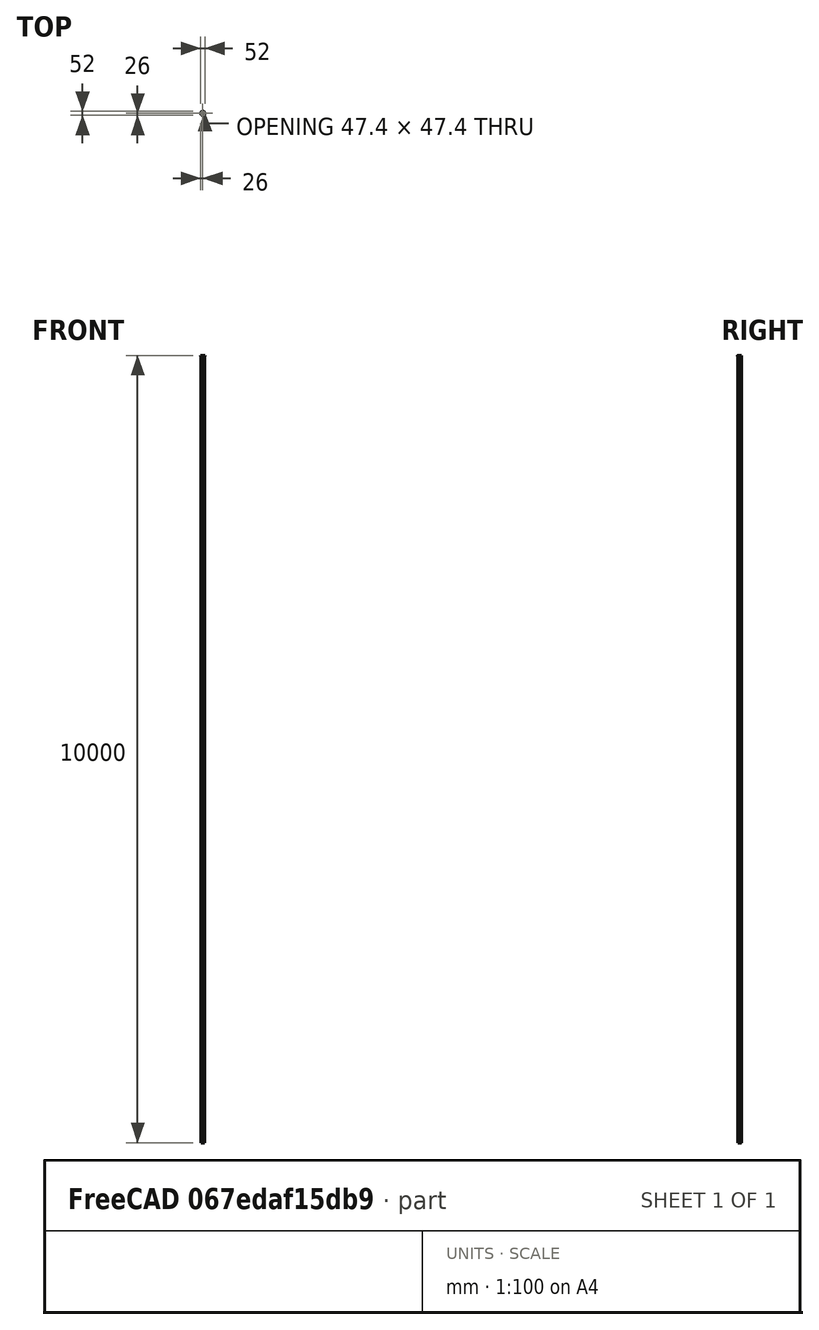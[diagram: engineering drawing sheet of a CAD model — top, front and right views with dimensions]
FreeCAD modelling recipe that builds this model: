
FCSTD DOCUMENT  (FreeCAD 0.16R)
Label: FWspacer
License: All rights reserved
LicenseURL: http://en.wikipedia.org/wiki/All_rights_reserved
objects: Sketcher::SketchObject×3, PartDesign::Pad×2, PartDesign::Pocket×1, PartDesign::PolarPattern×1, Mesh::Feature×1
note: 10 computed .brp shape members not serialized (recipe doc carries the construction recipe); baked Part::Feature solids carry a one-line shape summary decoded from their .brp

FEATURE [Sketcher::SketchObject] Sketch
  sketch-geometry (1):
    g0: Circle CenterX=0 CenterY=0 CenterZ=0 NormalX=0 NormalY=0 NormalZ=1 Radius=26
  constraints (2):
    c: Coincident(g0,g-1)
    c: Radius(g0) = 26
FEATURE [PartDesign::Pad] Pad
  Length = 5
  Length2 = 100
  Sketch = -> Sketch
  Type = 0
FEATURE [Sketcher::SketchObject] Sketch001
  Placement = pos=(0,0,5) rot=(0,0,1;0rad)
  Support = -> Pad [Face3]
  sketch-geometry (1):
    g0: Circle CenterX=0 CenterY=0 CenterZ=0 NormalX=0 NormalY=0 NormalZ=1 Radius=22.7
  constraints (2):
    c: Coincident(g0,g-1)
    c: Radius(g0) = 22.7
FEATURE [PartDesign::Pocket] Pocket
  Length = 5
  Sketch = -> Sketch001
  Type = 1
FEATURE [Sketcher::SketchObject] Sketch002
  ExternalGeometry = -> [Pocket]
  Placement = pos=(0,0,5) rot=(0,0,1;0rad)
  Support = -> Pocket [Face3]
  sketch-geometry (12):
    g0: LineSegment StartX=1.49899 StartY=22.4905 StartZ=0 EndX=1.49899 EndY=22.0946 EndZ=0
    g1: LineSegment StartX=1.10438 StartY=21.7 StartZ=0 EndX=-1.09517 EndY=21.7 EndZ=0
    g2: LineSegment StartX=-1.50098 StartY=22.1058 StartZ=0 EndX=-1.50098 EndY=22.3048 EndZ=0
    g3: LineSegment StartX=-1.89617 StartY=22.7 StartZ=0 EndX=-3 EndY=22.7 EndZ=0
    g4: LineSegment StartX=3 StartY=22.7 StartZ=0 EndX=3 EndY=23.7 EndZ=0
    g5: LineSegment StartX=3 StartY=23.7 StartZ=0 EndX=-3 EndY=23.7 EndZ=0
    g6: LineSegment StartX=-3 StartY=23.7 StartZ=0 EndX=-3 EndY=22.7 EndZ=0
    g7: LineSegment StartX=1.70847 StartY=22.7 StartZ=0 EndX=3 EndY=22.7 EndZ=0
    g8: ArcOfCircle CenterX=-1.89617 CenterY=22.3048 CenterZ=0 NormalX=0 NormalY=0 NormalZ=1 Radius=0.39519 StartAngle=0 EndAngle=1.5708
    g9: ArcOfCircle CenterX=1.70847 CenterY=22.4905 CenterZ=0 NormalX=0 NormalY=0 NormalZ=1 Radius=0.209471 StartAngle=1.5708 EndAngle=3.14159
    g10: ArcOfCircle CenterX=-1.09517 CenterY=22.1058 CenterZ=0 NormalX=0 NormalY=0 NormalZ=1 Radius=0.405815 StartAngle=3.14159 EndAngle=4.71239
    g11: ArcOfCircle CenterX=1.10438 CenterY=22.0946 CenterZ=0 NormalX=0 NormalY=0 NormalZ=1 Radius=0.394618 StartAngle=4.71239 EndAngle=6.28319
  constraints (26):
    c: Horizontal(g1)
    c: Vertical(g0)
    c: Vertical(g2)
    c: Horizontal(g3)
    c: Vertical(g4)
    c: Coincident(g4,g5)
    c: Horizontal(g5)
    c: Coincident(g5,g6)
    c: Coincident(g6,g3)
    c: Vertical(g6)
    c: Distance(g5) = 6
    c: Coincident(g7,g4)
    c: Horizontal(g7)
    c: Symmetric(g4,g3,g-2)
    c: Tangent(g7,g-3)
    c: Distance(g4) = 1
    c: Tangent(g3,g8) = -1.5708
    c: Tangent(g2,g8) = -1.5708
    c: Tangent(g0,g9) = -1.5708
    c: Tangent(g7,g9) = 1.5708
    c: Tangent(g1,g10) = 1.5708
    c: Tangent(g2,g10) = 1.5708
    c: Tangent(g1,g11) = 1.5708
    c: Tangent(g0,g11) = 1.5708
    c: Distance(g1,g7) = 1
    c: Distance(g2,g0) = 3
FEATURE [PartDesign::Pad] Pad001
  Length = 5
  Length2 = 100
  Reversed = true
  Sketch = -> Sketch002
  Type = 0
FEATURE [PartDesign::PolarPattern] PolarPattern
  Angle = 360
  Axis = -> Sketch002 [N_Axis]
  Occurrences = 12
  Originals = -> [Pad001]
FEATURE [Mesh::Feature] Mesh  label="PolarPattern (Meshed)"
